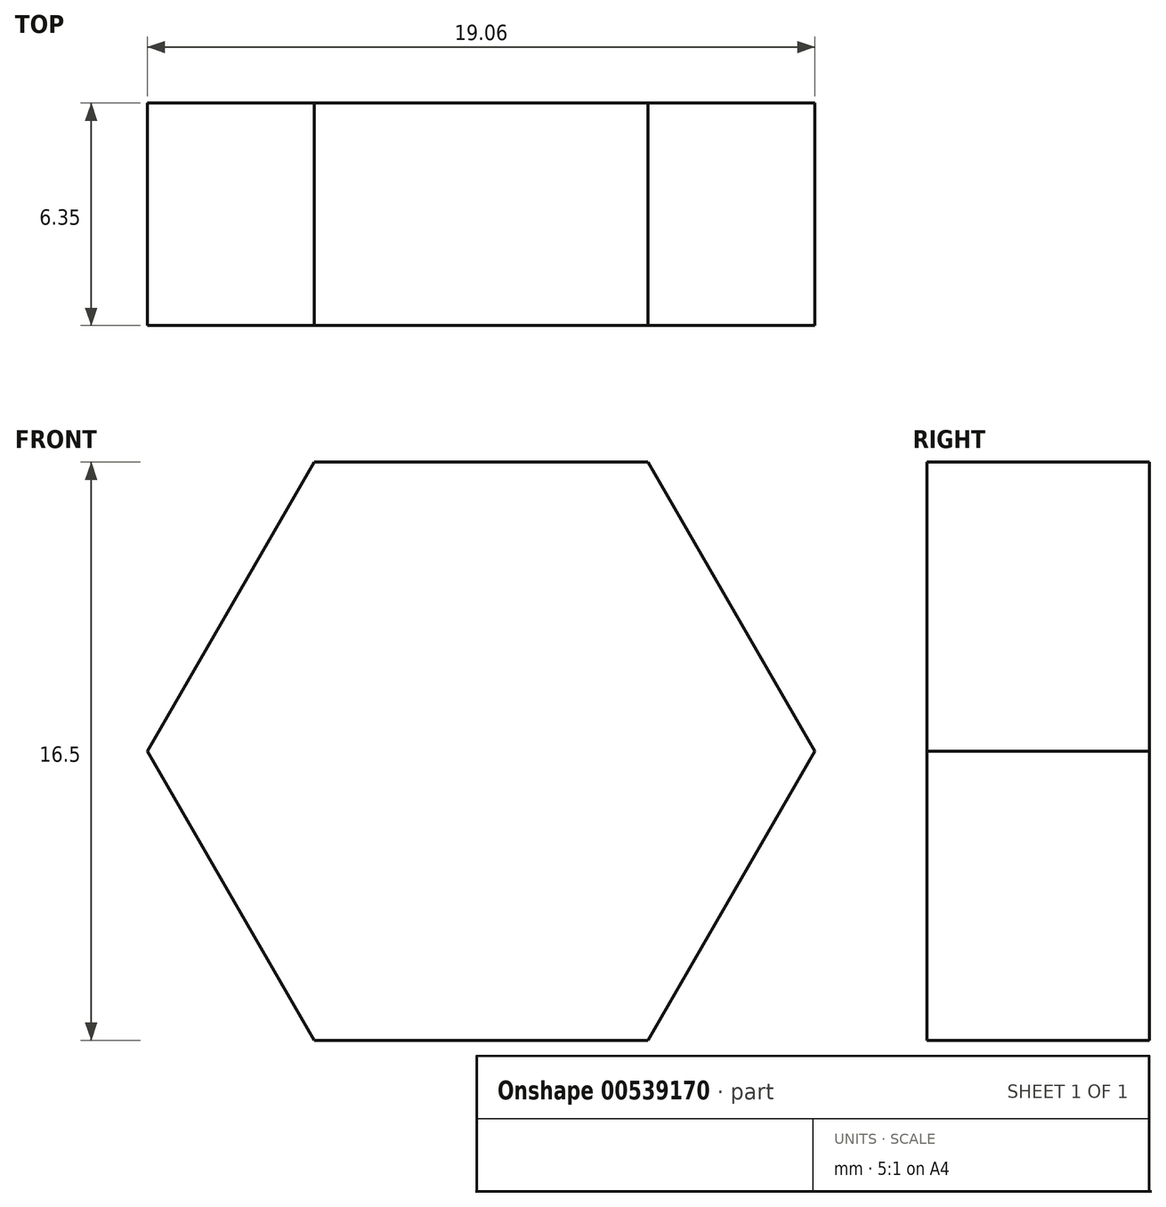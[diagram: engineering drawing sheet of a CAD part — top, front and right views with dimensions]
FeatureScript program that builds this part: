
annotation { "Feature Type Name" : "Feature", "Feature Type Description" : "" }
export const myFeature = defineFeature(function(context is Context, id is Id, definition is map)
    precondition{}
    {
        {
            var Q0;
            Q0=qCreatedBy(makeId("Front.planeOp"),FACE);
            var sketch = newSketch(context, id + "F0", { "sketchPlane" : qUnion([Q0])});
            skCircle(sketch, "E0.cCircle", {"center": v(0, 0) * mm, "radius": 8.25 * mm, "construction": true});
            skLineSegment(sketch, "E0.0", {"start": v(4.76, -8.25) * mm, "end": v(-4.76, -8.25) * mm});
            skLineSegment(sketch, "E0.1", {"start": v(-4.76, -8.25) * mm, "end": v(-9.53, 0) * mm});
            skLineSegment(sketch, "E0.2", {"start": v(-9.53, 0) * mm, "end": v(-4.76, 8.25) * mm});
            skLineSegment(sketch, "E0.3", {"start": v(-4.76, 8.25) * mm, "end": v(4.76, 8.25) * mm});
            skLineSegment(sketch, "E0.4", {"start": v(4.76, 8.25) * mm, "end": v(9.53, 0) * mm});
            skLineSegment(sketch, "E0.5", {"start": v(9.53, 0) * mm, "end": v(4.76, -8.25) * mm});
            skPoint(sketch, "E0.0.midPoint", {"position": v(0, -8.25) * mm});
            skSolve(sketch);
        }
        {
            var Q0;
            Q0=makeQuery(id+"F0.imprint","IMPRINT",FACE,{"disambiguationData":[TD([[makeQuery(id+"F0.imprint","IMPRINT",EDGE,{"derivedFrom":sQuery(id+"F0.wireOp",EDGE,"E0.0")}),-1.0]])]});
            extrude(context, id + "F1", {"entities" : qUnion([Q0]), "depth" : 6.35 * mm, "offsetDistance" : 25.4 * mm});
        }
        {
            var Q0;
            Q0=qCreatedBy(makeId("Front.planeOp"),FACE);
            var sketch = newSketch(context, id + "F2", { "sketchPlane" : qUnion([Q0])});
            skCircle(sketch, "E1", {"center": v(0, 0) * mm, "radius": 4.76 * mm});
            skSolve(sketch);
        }
        {
            var Q0;
            Q0=sQuery(id+"F2.wireOp",EDGE,"E1");
            extrude(context, id + "F3", {"bodyType" : ToolBodyType.SURFACE, "surfaceEntities" : qUnion([Q0]), "depth" : 38.1 * mm, "offsetDistance" : 25.4 * mm});
        }
    });
